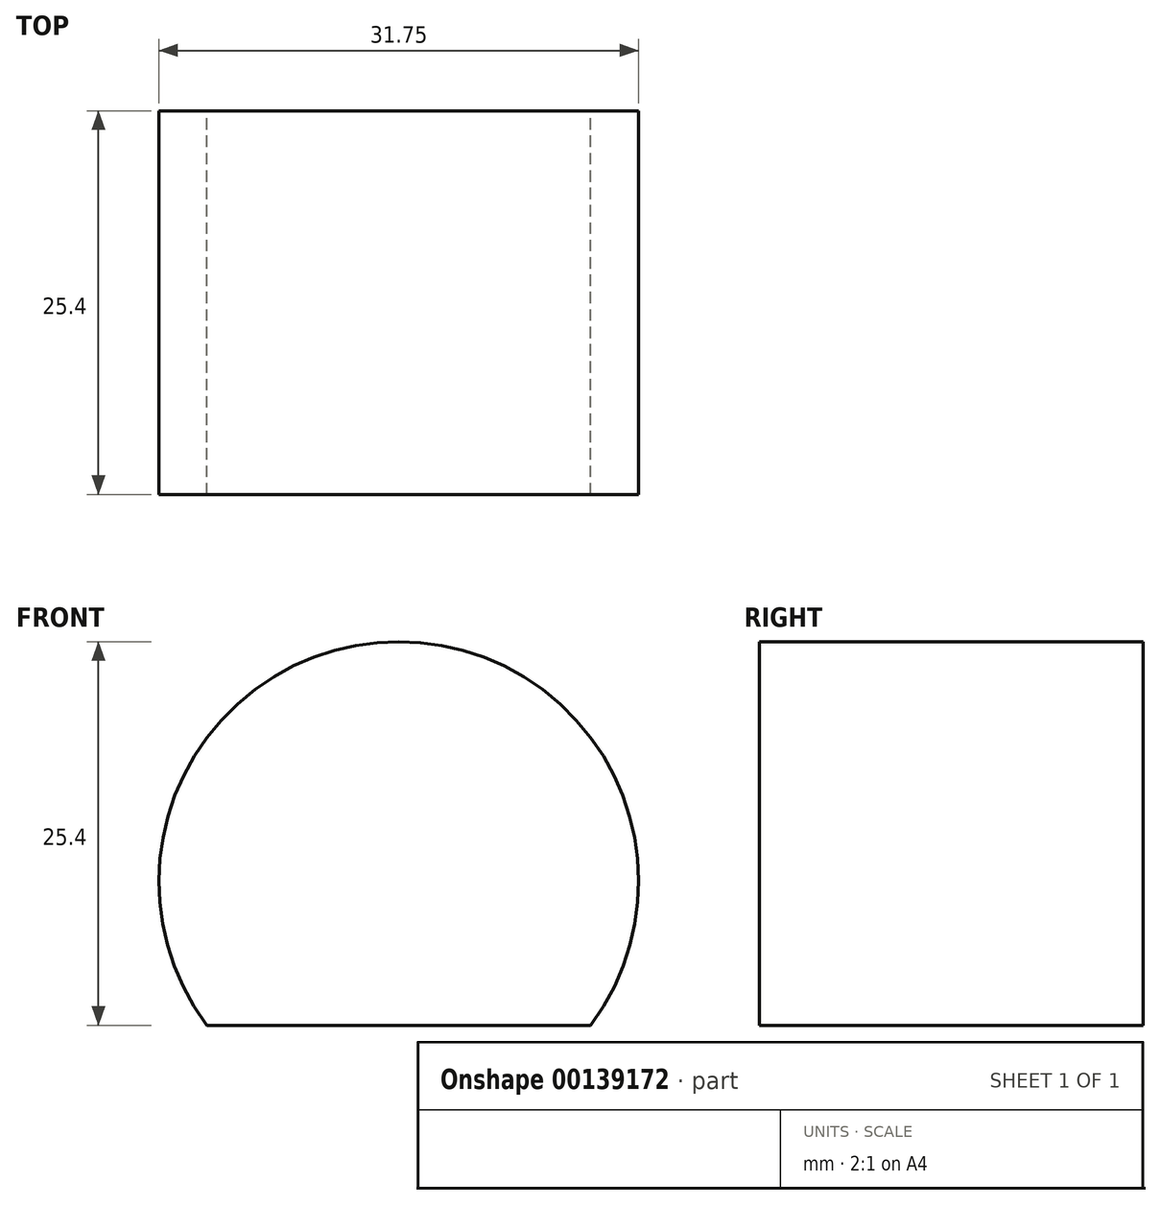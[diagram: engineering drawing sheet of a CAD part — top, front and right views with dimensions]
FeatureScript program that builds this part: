
annotation { "Feature Type Name" : "Feature", "Feature Type Description" : "" }
export const myFeature = defineFeature(function(context is Context, id is Id, definition is map)
    precondition{}
    {
        {
            var Q0;
            Q0=qCreatedBy(makeId("Front.planeOp"),FACE);
            var sketch = newSketch(context, id + "F0", { "sketchPlane" : qUnion([Q0])});
            skLineSegment(sketch, "E0", {"start": v(0, 0) * mm, "end": v(25.4, 0) * mm});
            skArc(sketch, "E1", {"start": v(25.4, 0) * mm, "mid": v(12.7, 25.4) * mm, "end": v(0, 0) * mm});
            skSolve(sketch);
        }
        {
            var Q0;
            Q0=qSketchRegion(id+"F0",true);
            extrude(context, id + "F1", {"entities" : qUnion([Q0]), "depth" : 25.4 * mm});
        }
    });
